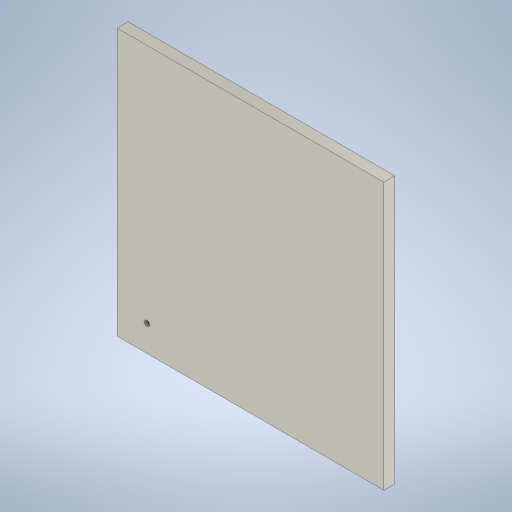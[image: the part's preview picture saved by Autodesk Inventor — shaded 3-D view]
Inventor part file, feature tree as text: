
AUTODESK INVENTOR PART (.ipt)
format: ipt  version: 2023 (Build 270158000, 158)  size: 204,288 bytes
history: native  units: in
note: dims shown in document units (in); Inventor stores cm internally (conversion verified against a paired STEP export)
features: sketch x2, extrude x1, hole x1
ambient origin geometry x8: Origin, YZ Plane, XZ Plane, XY Plane, X Axis, Y Axis, Z Axis, Center Point
bodies: Solid1 (feature_tree)
feature tree (4):
  extrude  "Extrusion1"  Depth=3.8189in
  hole  "Hole1"  [1 undecoded]
  sketch  "Sketch1"  dims[d0=3.8189in d1=3.8189in]
  sketch  "Sketch2"  dims[d2=0.1575in d3=0.0in d4=0.0787in d5=0.2362in d6=0.1575in d7=0.0787in d8=90.0deg d9=0.315in d10=0.8108in]
note: 1 required parameter value undecoded (feature->parameter linkage not recoverable at this tier; creation-order binding heuristic only, values carry confidence <= 0.55)
